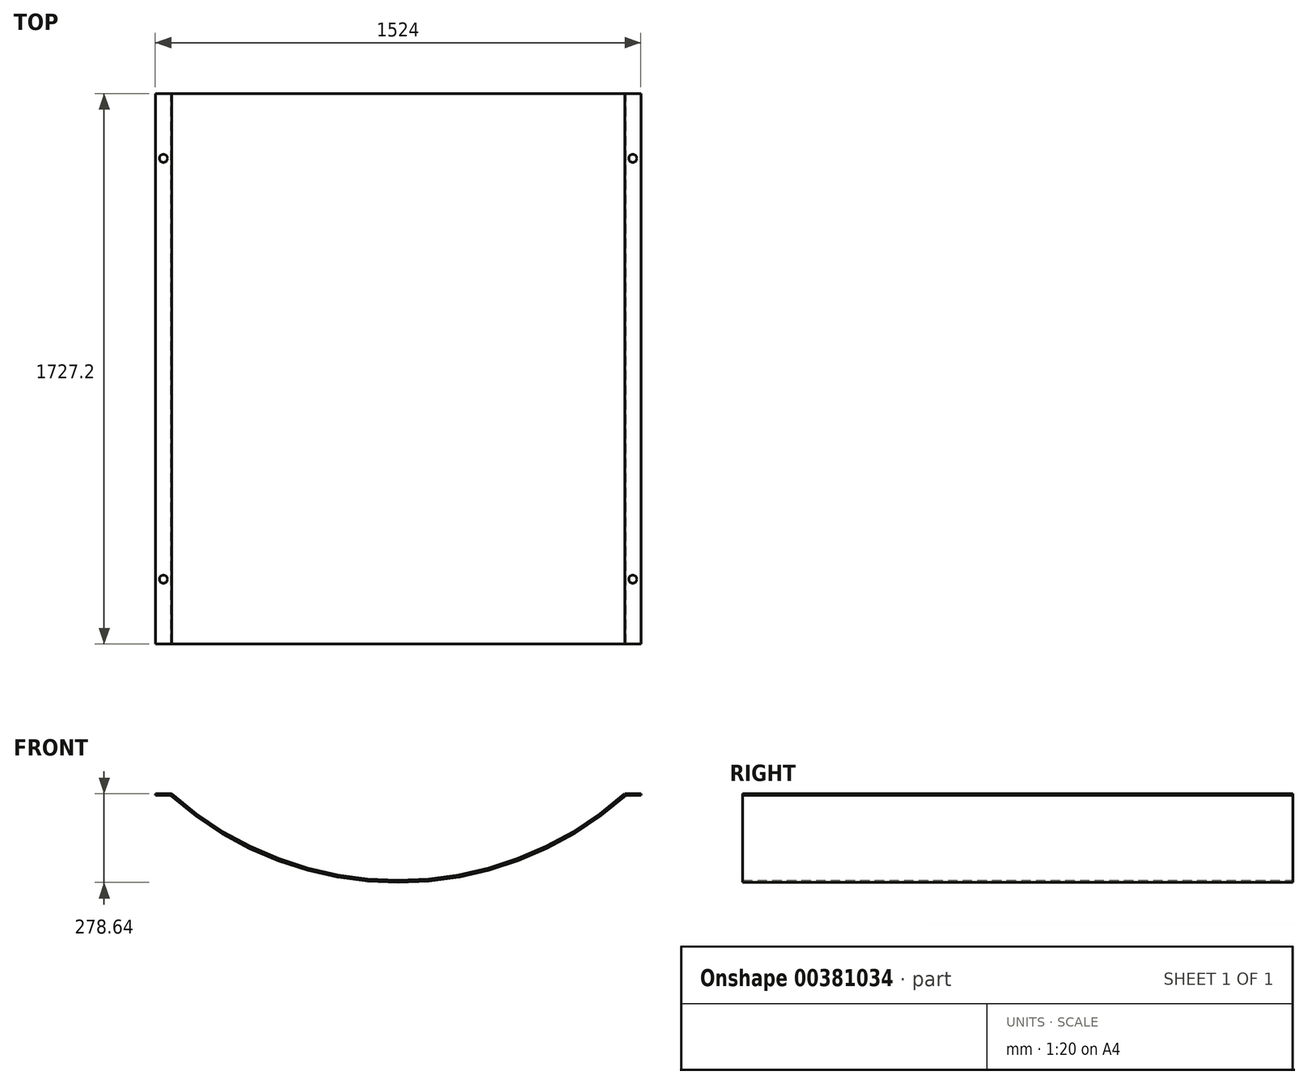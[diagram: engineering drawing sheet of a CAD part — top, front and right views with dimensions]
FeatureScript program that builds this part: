
annotation { "Feature Type Name" : "Feature", "Feature Type Description" : "" }
export const myFeature = defineFeature(function(context is Context, id is Id, definition is map)
    precondition{}
    {
        {
            var Q0;
            Q0=qCreatedBy(makeId("Front.planeOp"),FACE);
            var sketch = newSketch(context, id + "F0", { "sketchPlane" : qUnion([Q0])});
            skArc(sketch, "E0", {"start": v(-437.48, 381.66) * mm, "mid": v(273.73, 109.97) * mm, "end": v(984.92, 381.71) * mm});
            skLineSegment(sketch, "E1", {"start": v(984.92, 381.71) * mm, "end": v(989.83, 377.67) * mm});
            skLineSegment(sketch, "E2", {"start": v(-437.48, 381.66) * mm, "end": v(-439.72, 375.72) * mm});
            skArc(sketch, "E3", {"start": v(-439.72, 375.72) * mm, "mid": v(275.43, 103.07) * mm, "end": v(989.83, 377.67) * mm});
            skLineSegment(sketch, "E4", {"start": v(984.92, 381.71) * mm, "end": v(1035.72, 381.71) * mm});
            skLineSegment(sketch, "E5", {"start": v(1035.72, 381.71) * mm, "end": v(1035.72, 376.8) * mm});
            skLineSegment(sketch, "E6", {"start": v(1035.72, 376.8) * mm, "end": v(988.85, 376.8) * mm});
            skLineSegment(sketch, "E7", {"start": v(-437.48, 381.66) * mm, "end": v(-488.28, 381.66) * mm});
            skLineSegment(sketch, "E8", {"start": v(-488.28, 381.66) * mm, "end": v(-488.28, 376.73) * mm});
            skLineSegment(sketch, "E9", {"start": v(-488.28, 376.73) * mm, "end": v(-439.72, 375.72) * mm});
            skSolve(sketch);
        }
        {
            var Q0;
            Q0 = qSketchRegion(id + "F0", true);
            extrude(context, id + "F1", {"entities" : qUnion([Q0]), "depth" : 1727.2 * mm});
        }
        {
            var Q0;
            Q0=qCreatedBy(makeId("Top.planeOp"),FACE);
            var sketch = newSketch(context, id + "F2", { "sketchPlane" : qUnion([Q0])});
            skCircle(sketch, "E10", {"center": v(-462.88, -203.2) * mm, "radius": 9.53 * mm});
            skCircle(sketch, "E11", {"center": v(1010.32, -203.2) * mm, "radius": 9.53 * mm});
            skCircle(sketch, "E12", {"center": v(1010.32, -1524) * mm, "radius": 9.53 * mm});
            skCircle(sketch, "E13", {"center": v(-462.88, -1524) * mm, "radius": 9.53 * mm});
            skSolve(sketch);
        }
        {
            var Q0;
            Q0=sQuery(id+"F2.wireOp",VERTEX,"E11.center");
            var Q1;
            Q1=sQuery(id+"F2.wireOp",VERTEX,"E12.center");
            var Q2;
            Q2=sQuery(id+"F2.wireOp",VERTEX,"E13.center");
            var Q3;
            Q3=sQuery(id+"F2.wireOp",VERTEX,"E10.center");
            var Q4;
            Q4=makeQuery(id+"F1.opExtrude","SWEPT_BODY",BODY,{"disambiguationData":[OSD([sQuery(id+"F0.wireOp",EDGE,"E0"),sQuery(id+"F0.wireOp",EDGE,"E3"),sQuery(id+"F0.wireOp",EDGE,"E4"),sQuery(id+"F0.wireOp",EDGE,"E5"),sQuery(id+"F0.wireOp",EDGE,"E6"),sQuery(id+"F0.wireOp",EDGE,"E7"),sQuery(id+"F0.wireOp",EDGE,"E8"),sQuery(id+"F0.wireOp",EDGE,"E9")])]});
            hole(context, id + "F3", {"style" : HoleStyle.SIMPLE, "endStyle" : HoleEndStyle.THROUGH, "oppositeDirection" : true, "holeDiameter" : 25.4 * mm, "isTappedThrough" : true, "tappedDepth" : 12.7 * mm, "tapClearance" : 3, "startFromSketch" : true, "locations" : qUnion([Q0, Q1, Q2, Q3]), "scope" : qUnion([Q4])});
        }
    });
